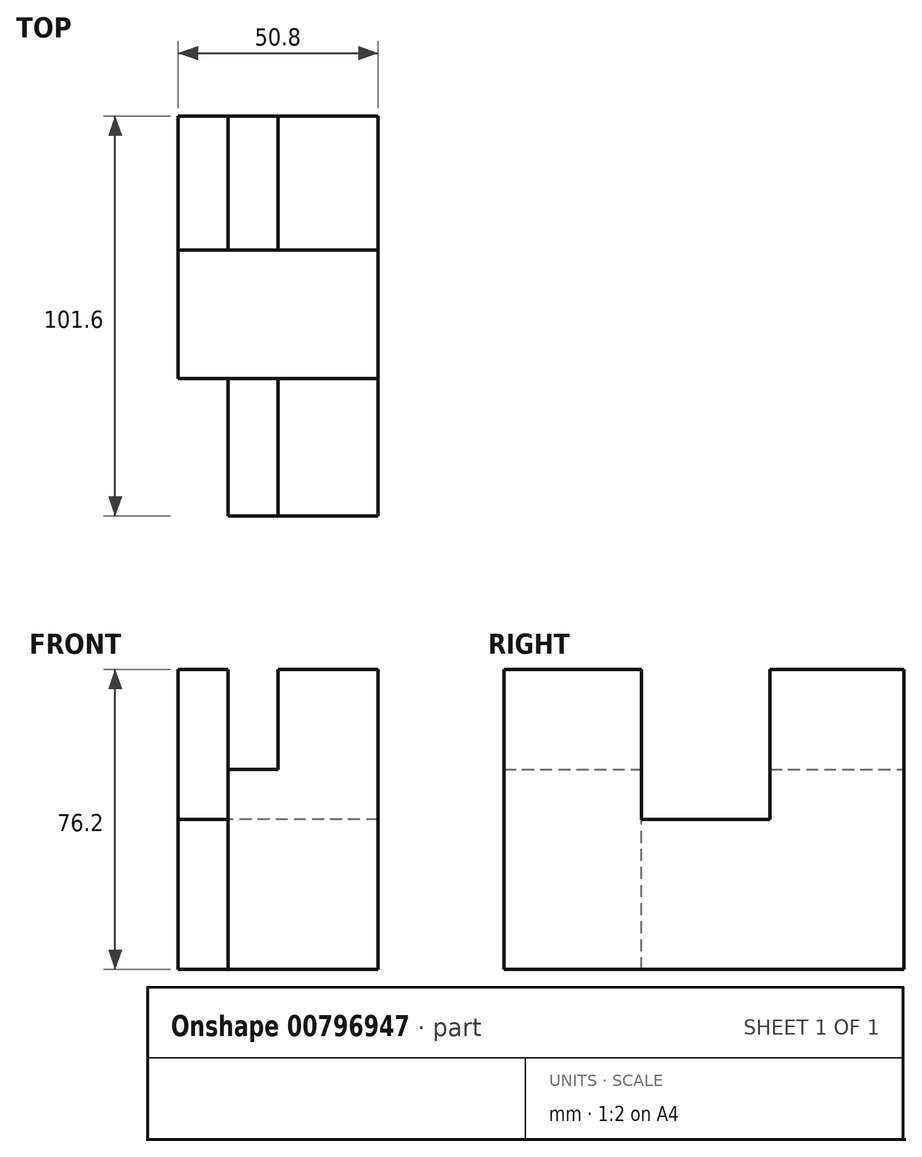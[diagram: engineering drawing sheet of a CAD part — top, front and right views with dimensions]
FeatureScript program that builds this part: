
annotation { "Feature Type Name" : "Feature", "Feature Type Description" : "" }
export const myFeature = defineFeature(function(context is Context, id is Id, definition is map)
    precondition{}
    {
        {
            var Q0;
            Q0=qCreatedBy(makeId("Top.planeOp"),FACE);
            var sketch = newSketch(context, id + "F0", { "sketchPlane" : qUnion([Q0])});
            skLineSegment(sketch, "E0.bottom", {"start": v(-76.2, 50.8) * mm, "end": v(76.2, 50.8) * mm});
            skLineSegment(sketch, "E0.top", {"start": v(-76.2, -50.8) * mm, "end": v(76.2, -50.8) * mm});
            skLineSegment(sketch, "E0.left", {"start": v(-76.2, 50.8) * mm, "end": v(-76.2, -50.8) * mm});
            skLineSegment(sketch, "E0.right", {"start": v(76.2, 50.8) * mm, "end": v(76.2, -50.8) * mm});
            skPoint(sketch, "E0.middle", {"position": v(0, 0) * mm});
            skSolve(sketch);
        }
        {
            var Q0;
            Q0=makeQuery(id+"F0.imprint","IMPRINT",FACE,{"disambiguationData":[TD([[makeQuery(id+"F0.imprint","IMPRINT",EDGE,{"derivedFrom":sQuery(id+"F0.wireOp",EDGE,"E0.bottom")}),-1.0]])]});
            extrude(context, id + "F1", {"entities" : qUnion([Q0]), "depth" : 76.2 * mm, "offsetDistance" : 25.4 * mm, "symmetric" : true});
        }
        {
            var Q0;
            Q0=makeQuery(id+"F1.opExtrude","CAP_FACE",FACE,{"disambiguationData":[OSD([sQuery(id+"F0.wireOp",EDGE,"E0.bottom"),sQuery(id+"F0.wireOp",EDGE,"E0.top"),sQuery(id+"F0.wireOp",EDGE,"E0.left"),sQuery(id+"F0.wireOp",EDGE,"E0.right")])],"isStart":false});
            var sketch = newSketch(context, id + "F2", { "sketchPlane" : qUnion([Q0])});
            skLineSegment(sketch, "E1.bottom", {"start": v(38.1, -50.8) * mm, "end": v(50.8, -50.8) * mm});
            skLineSegment(sketch, "E1.top", {"start": v(38.1, 50.8) * mm, "end": v(50.8, 50.8) * mm});
            skLineSegment(sketch, "E1.left", {"start": v(38.1, -50.8) * mm, "end": v(38.1, 50.8) * mm});
            skLineSegment(sketch, "E1.right", {"start": v(50.8, -50.8) * mm, "end": v(50.8, 50.8) * mm});
            skSolve(sketch);
        }
        {
            var Q0;
            Q0 = qSketchRegion(id + "F2", true);
            extrude(context, id + "F3", {"entities" : qUnion([Q0]), "operationType" : NewBodyOperationType.REMOVE, "oppositeDirection" : true, "depth" : 25.4 * mm, "offsetDistance" : 25.4 * mm});
        }
        {
            var Q0;
            {var subQ0=sQuery(id+"F0.wireOp",EDGE,"E0.bottom");var subQ1=sQuery(id+"F0.wireOp",EDGE,"E0.top");var subQ2=sQuery(id+"F0.wireOp",EDGE,"E0.left");Q0=makeQuery(id+"F3.boolean.opBoolean","SPLIT",FACE,{"disambiguationData":[TD([makeQuery(id+"F1.opExtrude","SWEPT_FACE",FACE,{"disambiguationData":[OSD([subQ2])]})])],"derivedFrom":makeQuery(id+"F1.opExtrude","CAP_FACE",FACE,{"disambiguationData":[OSD([subQ0,subQ1,subQ2,sQuery(id+"F0.wireOp",EDGE,"E0.right")])],"isStart":false})});}
            var sketch = newSketch(context, id + "F4", { "sketchPlane" : qUnion([Q0])});
            skLineSegment(sketch, "E2.bottom", {"start": v(76.2, 16.76) * mm, "end": v(-76.2, 16.76) * mm});
            skLineSegment(sketch, "E2.top", {"start": v(76.2, -15.92) * mm, "end": v(-76.2, -15.92) * mm});
            skLineSegment(sketch, "E2.left", {"start": v(76.2, 16.76) * mm, "end": v(76.2, -15.92) * mm});
            skLineSegment(sketch, "E2.right", {"start": v(-76.2, 16.76) * mm, "end": v(-76.2, -15.92) * mm});
            skLineSegment(sketch, "E3.0", {"start": v(76.2, 50.8) * mm, "end": v(76.2, -50.8) * mm});
            skSolve(sketch);
        }
        {
            var Q0;
            Q0 = qSketchRegion(id + "F4", true);
            extrude(context, id + "F5", {"entities" : qUnion([Q0]), "operationType" : NewBodyOperationType.REMOVE, "oppositeDirection" : true, "depth" : 38.1 * mm, "offsetDistance" : 25.4 * mm});
        }
        {
            var Q0;
            {var subQ0=sQuery(id+"F0.wireOp",EDGE,"E0.top");var subQ1=makeQuery(id+"F1.opExtrude","SWEPT_FACE",FACE,{"disambiguationData":[OSD([subQ0])]});var subQ2=sQuery(id+"F0.wireOp",EDGE,"E0.left");var subQ3=makeQuery(id+"F1.opExtrude","SWEPT_FACE",FACE,{"disambiguationData":[OSD([subQ2])]});var subQ5=sQuery(id+"F0.wireOp",EDGE,"E0.bottom");Q0=makeQuery(id+"F5.boolean.opBoolean","SPLIT",FACE,{"disambiguationData":[TD([subQ1])],"derivedFrom":makeQuery(id+"F3.boolean.opBoolean","SPLIT",FACE,{"disambiguationData":[TD([subQ3])],"derivedFrom":makeQuery(id+"F1.opExtrude","CAP_FACE",FACE,{"disambiguationData":[OSD([subQ5,subQ0,subQ2,sQuery(id+"F0.wireOp",EDGE,"E0.right")])],"isStart":false})})});}
            var sketch = newSketch(context, id + "F6", { "sketchPlane" : qUnion([Q0])});
            skLineSegment(sketch, "E4.bottom", {"start": v(25.4, -50.8) * mm, "end": v(76.2, -50.8) * mm});
            skLineSegment(sketch, "E4.top", {"start": v(25.4, 50.8) * mm, "end": v(76.2, 50.8) * mm});
            skLineSegment(sketch, "E4.left", {"start": v(25.4, -50.8) * mm, "end": v(25.4, 50.8) * mm});
            skLineSegment(sketch, "E4.right", {"start": v(76.2, -50.8) * mm, "end": v(76.2, 50.8) * mm});
            skLineSegment(sketch, "E5.0", {"start": v(50.8, 50.8) * mm, "end": v(76.2, 50.8) * mm});
            skSolve(sketch);
        }
        {
            var Q0;
            {var subQ1=sQuery(id+"F6.wireOp",EDGE,"E4.top");Q0=makeQuery(id+"F6.imprint","IMPRINT",FACE,{"disambiguationData":[TD([[makeQuery(id+"F6.imprint","IMPRINT",EDGE,{"derivedFrom":subQ1}),-1.0]])]});}
            var Q1;
            {var subQ2=sQuery(id+"F0.wireOp",EDGE,"E0.top");var subQ4=makeQuery(id+"F1.opExtrude","SWEPT_FACE",FACE,{"disambiguationData":[OSD([subQ2])]});var subQ5=sQuery(id+"F2.wireOp",EDGE,"E1.left");var subQ10=makeQuery(id+"F5.boolean.opBoolean","SPLIT",EDGE,{"disambiguationData":[TD([subQ4])],"derivedFrom":makeQuery(id+"F3.boolean.opBoolean","COPY",EDGE,{"derivedFrom":makeQuery(id+"F3.opExtrude","CAP_EDGE",EDGE,{"disambiguationData":[OSD([subQ5])],"isStart":true})})});Q1=makeQuery(id+"F6.imprint","IMPRINT",FACE,{"disambiguationData":[TD([[makeQuery(id+"F6.imprint","IMPRINT",EDGE,{"derivedFrom":subQ10}),1.0]])]});}
            extrude(context, id + "F7", {"entities" : qUnion([Q0, Q1]), "operationType" : NewBodyOperationType.INTERSECT, "endBound" : BoundingType.THROUGH_ALL, "oppositeDirection" : true, "depth" : 25.4 * mm, "offsetDistance" : 25.4 * mm});
        }
    });
